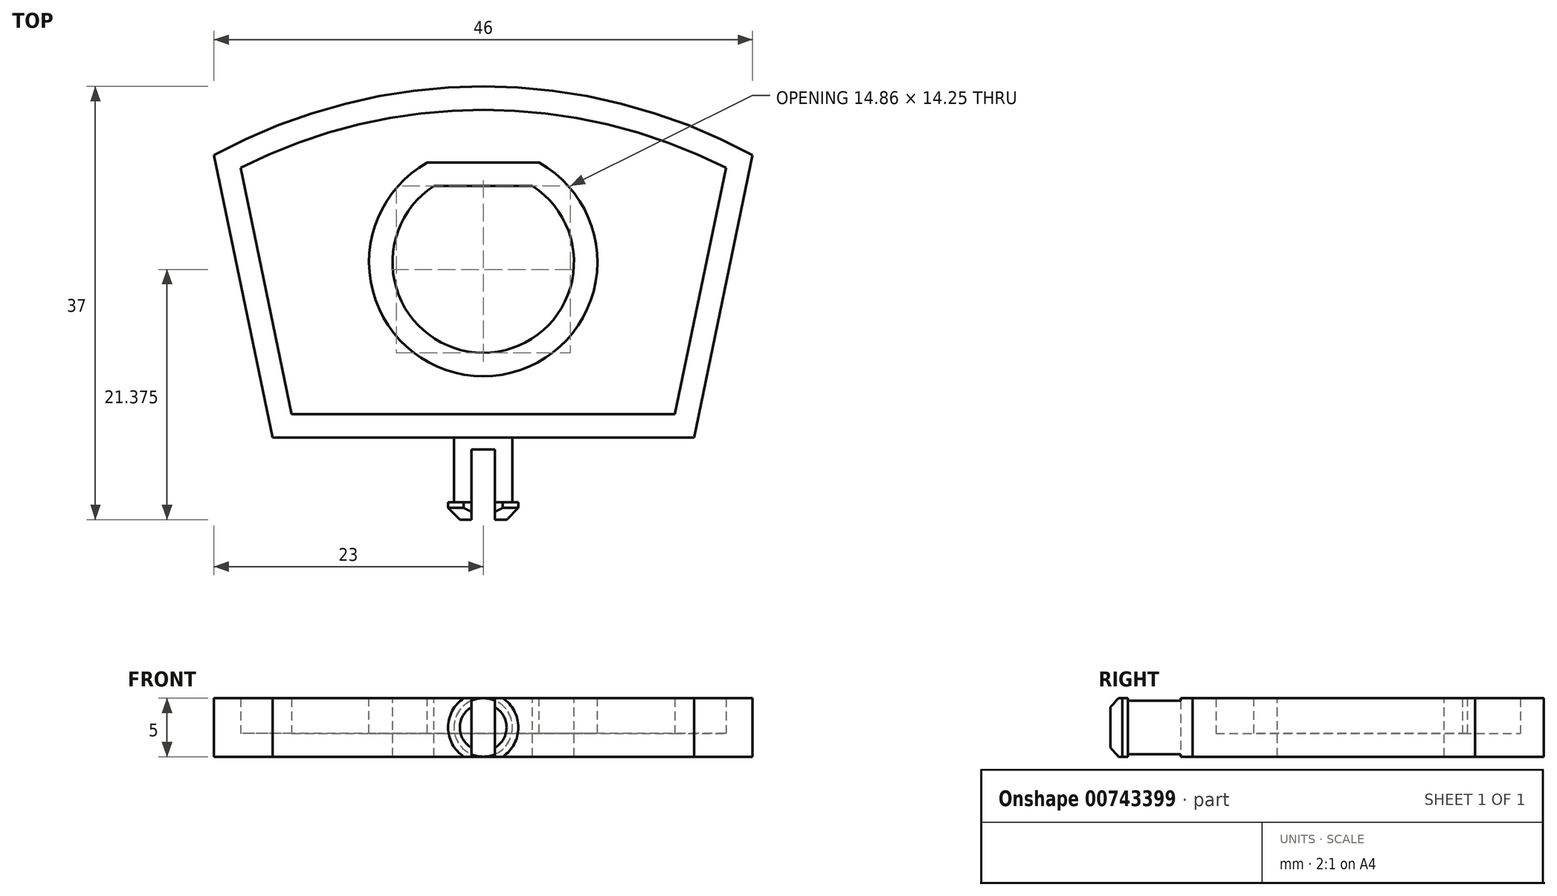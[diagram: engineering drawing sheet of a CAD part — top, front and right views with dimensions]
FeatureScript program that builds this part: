
annotation { "Feature Type Name" : "Feature", "Feature Type Description" : "" }
export const myFeature = defineFeature(function(context is Context, id is Id, definition is map)
    precondition{}
    {
        {
            var Q0;
            Q0=qCreatedBy(makeId("Top.planeOp"),FACE);
            var sketch = newSketch(context, id + "F0", { "sketchPlane" : qUnion([Q0])});
            skLineSegment(sketch, "E0", {"start": v(-18, 0) * mm, "end": v(18, 0) * mm});
            skLineSegment(sketch, "E1", {"start": v(18, 0) * mm, "end": v(23, 24.13) * mm});
            skLineSegment(sketch, "E2", {"start": v(-18, 0) * mm, "end": v(-23, 24.13) * mm});
            skArc(sketch, "E3", {"start": v(23, 24.13) * mm, "mid": v(0, 30) * mm, "end": v(-23, 24.13) * mm});
            skLineSegment(sketch, "E4", {"start": v(0, 30) * mm, "end": v(0, 0) * mm, "construction": true});
            skSolve(sketch);
        }
        {
            var Q0;
            Q0=makeQuery(id+"F0.imprint","IMPRINT",FACE,{"disambiguationData":[TD([[makeQuery(id+"F0.imprint","IMPRINT",EDGE,{"derivedFrom":sQuery(id+"F0.wireOp",EDGE,"E0")}),1.0]])]});
            extrude(context, id + "F1", {"entities" : qUnion([Q0]), "endBound" : BoundingType.SYMMETRIC, "depth" : 5 * mm, "offsetDistance" : 25 * mm});
        }
        {
            var Q0;
            Q0=makeQuery(id+"F1.opExtrude","CAP_FACE",FACE,{"disambiguationData":[OSD([sQuery(id+"F0.wireOp",EDGE,"E0"),sQuery(id+"F0.wireOp",EDGE,"E1"),sQuery(id+"F0.wireOp",EDGE,"E2"),sQuery(id+"F0.wireOp",EDGE,"E3")])],"isStart":false});
            var sketch = newSketch(context, id + "F2", { "sketchPlane" : qUnion([Q0])});
            skLineSegment(sketch, "E5", {"start": v(-4.22, 21.5) * mm, "end": v(4.22, 21.5) * mm});
            skArc(sketch, "E6", {"start": v(-4.22, 21.5) * mm, "mid": v(0, 7.25) * mm, "end": v(4.22, 21.5) * mm});
            skSolve(sketch);
        }
        {
            var Q0;
            Q0=makeQuery(id+"F2.imprint","IMPRINT",FACE,{"disambiguationData":[TD([[makeQuery(id+"F2.imprint","IMPRINT",EDGE,{"derivedFrom":sQuery(id+"F2.wireOp",EDGE,"E5")}),-1.0]])]});
            extrude(context, id + "F3", {"entities" : qUnion([Q0]), "operationType" : NewBodyOperationType.REMOVE, "endBound" : BoundingType.UP_TO_NEXT, "oppositeDirection" : true, "depth" : 25 * mm, "offsetDistance" : 25 * mm});
        }
        {
            var Q0;
            Q0=makeQuery(id+"F1.opExtrude","CAP_FACE",FACE,{"disambiguationData":[OSD([sQuery(id+"F0.wireOp",EDGE,"E0"),sQuery(id+"F0.wireOp",EDGE,"E1"),sQuery(id+"F0.wireOp",EDGE,"E2"),sQuery(id+"F0.wireOp",EDGE,"E3")])],"isStart":false});
            shell(context, id + "F4", {"entities" : qUnion([Q0]), "thickness" : 2 * mm});
        }
        {
            var Q0;
            Q0=qCreatedBy(makeId("Right.planeOp"),FACE);
            var sketch = newSketch(context, id + "F5", { "sketchPlane" : qUnion([Q0])});
            skLineSegment(sketch, "E7", {"start": v(0, 0) * mm, "end": v(-7, 0) * mm});
            skLineSegment(sketch, "E8", {"start": v(-7, 0) * mm, "end": v(-7, 3) * mm});
            skLineSegment(sketch, "E9", {"start": v(-7, 3) * mm, "end": v(-5.5, 3) * mm});
            skLineSegment(sketch, "E10", {"start": v(-5.5, 3) * mm, "end": v(-5.5, 2.5) * mm});
            skLineSegment(sketch, "E11", {"start": v(-5.5, 2.5) * mm, "end": v(0, 2.5) * mm});
            skLineSegment(sketch, "E12", {"start": v(0, 2.5) * mm, "end": v(0, 0) * mm});
            skSolve(sketch);
        }
        {
            var Q0;
            Q0 = qSketchRegion(id + "F5", true);
            var Q1;
            Q1=sQuery(id+"F5.wireOp",EDGE,"E7");
            revolve(context, id + "F6", {"operationType" : NewBodyOperationType.ADD, "surfaceOperationType" : NewSurfaceOperationType.NEW, "entities" : qUnion([Q0]), "axis" : qUnion([Q1]), "revolveType" : RevolveType.FULL});
        }
        {
            var Q0;
            Q0=makeQuery(id+"F6.opRevolve","SWEPT_FACE",FACE,{"disambiguationData":[OSD([sQuery(id+"F5.wireOp",EDGE,"E8")])]});
            chamfer(context, id + "F7", {"entities" : qUnion([Q0]), "width" : 1 * mm, "tangentPropagation" : true});
        }
        {
            var Q0;
            Q0=makeQuery(id+"F6.opRevolve","SWEPT_FACE",FACE,{"disambiguationData":[OSD([sQuery(id+"F5.wireOp",EDGE,"E8")])]});
            var sketch = newSketch(context, id + "F8", { "sketchPlane" : qUnion([Q0])});
            skLineSegment(sketch, "E13.bottom", {"start": v(-24, 2.5) * mm, "end": v(24.78, 2.5) * mm});
            skLineSegment(sketch, "E13.top", {"start": v(-24, -2.5) * mm, "end": v(24.78, -2.5) * mm});
            skLineSegment(sketch, "E13.left", {"start": v(-24, 2.5) * mm, "end": v(-24, -2.5) * mm});
            skLineSegment(sketch, "E13.right", {"start": v(24.78, 2.5) * mm, "end": v(24.78, -2.5) * mm});
            skSolve(sketch);
        }
        {
            var Q0;
            Q0 = qSketchRegion(id + "F8", true);
            extrude(context, id + "F9", {"entities" : qUnion([Q0]), "operationType" : NewBodyOperationType.INTERSECT, "endBound" : BoundingType.THROUGH_ALL, "oppositeDirection" : true, "depth" : 25 * mm, "offsetDistance" : 25 * mm});
        }
        {
            var Q0;
            Q0=makeQuery(id+"F6.opRevolve","SWEPT_FACE",FACE,{"disambiguationData":[OSD([sQuery(id+"F5.wireOp",EDGE,"E8")])]});
            var sketch = newSketch(context, id + "F10", { "sketchPlane" : qUnion([Q0])});
            skLineSegment(sketch, "E14.bottom", {"start": v(-1, 4.33) * mm, "end": v(1, 4.33) * mm});
            skLineSegment(sketch, "E14.top", {"start": v(-1, -4.37) * mm, "end": v(1, -4.37) * mm});
            skLineSegment(sketch, "E14.left", {"start": v(-1, 4.33) * mm, "end": v(-1, -4.37) * mm});
            skLineSegment(sketch, "E14.right", {"start": v(1, 4.33) * mm, "end": v(1, -4.37) * mm});
            skSolve(sketch);
        }
        {
            var Q0;
            Q0 = qSketchRegion(id + "F10", true);
            extrude(context, id + "F11", {"entities" : qUnion([Q0]), "operationType" : NewBodyOperationType.REMOVE, "oppositeDirection" : true, "depth" : 6 * mm, "offsetDistance" : 25 * mm});
        }
    });
